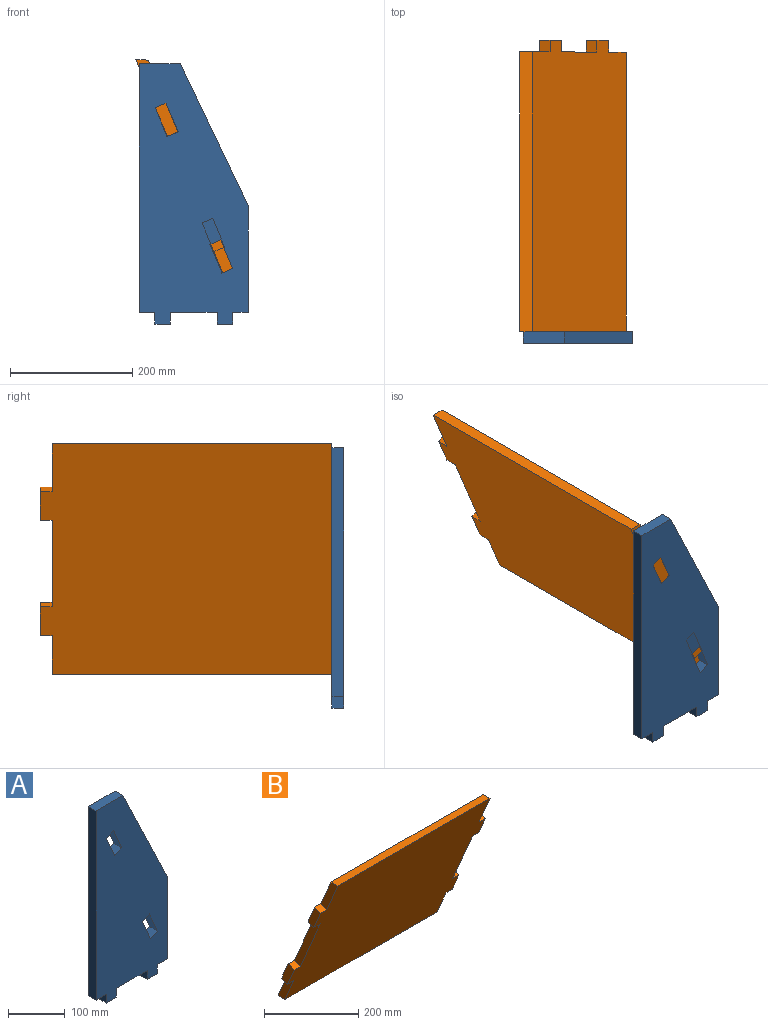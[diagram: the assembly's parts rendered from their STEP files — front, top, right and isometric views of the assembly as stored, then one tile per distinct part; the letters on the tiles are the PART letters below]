
ASSEMBLY  parts=2 mates=1
PART A: 23 faces, bbox 177.9x19.1x425.5 mm
  f0: plane 425.45x177.85mm, normal (0,-1,0), area 58405.1mm2, adj f2,f3,f4,f5,f6,f7,f8,f9
  f1: plane 425.45x177.85mm, normal (0,1,0), area 58405.1mm2, adj f2,f3,f4,f5,f6,f7,f8,f9
  f2: plane 76.25x19.05mm, normal (0,0,-1), area 1452.6mm2, adj f0,f1,f3,f14
  f3: plane 19.05x19.05mm, normal (-1,0,0), area 362.9mm2, adj f0,f1,f2,f4
  f4: plane 25.4x19.05mm, normal (0,0,-1), area 483.9mm2, adj f0,f1,f3,f5
  f5: plane 19.05x19.05mm, normal (1,0,0), area 362.9mm2, adj f0,f1,f4,f6
  f6: plane 25.4x19.05mm, normal (0,0,-1), area 483.9mm2, adj f0,f1,f5,f7
  f7: plane 174.24x19.05mm, normal (1,0,0), area 3319.3mm2, adj f0,f1,f6,f8
  f8: plane 232.16x111.15mm, normal (0.9,0,0.43), area 4903.3mm2, adj f0,f1,f7,f9
  f9: plane 66.7x19.05mm, normal (0,0,1), area 1270.6mm2, adj f0,f1,f8,f10
  f10: plane 406.4x19.05mm, normal (-1,0,0), area 7741.9mm2, adj f0,f1,f9,f11
  f11: plane 25.4x19.05mm, normal (0,0,-1), area 483.9mm2, adj f0,f1,f10,f12
  f12: plane 19.05x19.05mm, normal (-1,0,0), area 362.9mm2, adj f0,f1,f11,f13
  f13: plane 25.4x19.05mm, normal (0,0,-1), area 483.9mm2, adj f0,f1,f12,f14
  f14: plane 19.05x19.05mm, normal (1,0,0), area 362.9mm2, adj f0,f1,f2,f13
  f15: plane 46.81x19.73mm, normal (-0.92,0,-0.39), area 967.7mm2, adj f0,f1,f16,f18
  f16: plane 19.05x17.55mm, normal (0.39,0,-0.92), area 362.9mm2, adj f0,f1,f15,f17
  f17: plane 46.81x19.73mm, normal (0.92,0,0.39), area 967.7mm2, adj f0,f1,f16,f18
  f18: plane 19.05x17.55mm, normal (-0.39,0,0.92), area 362.9mm2, adj f0,f1,f15,f17
  f19: plane 46.66x20.09mm, normal (-0.92,0,-0.4), area 967.7mm2, adj f0,f1,f20,f22
  f20: plane 19.05x17.65mm, normal (0.38,0,-0.93), area 363mm2, adj f0,f1,f19,f21
  f21: plane 47.01x20.25mm, normal (0.92,0,0.4), area 975.1mm2, adj f0,f1,f20,f22
  f22: plane 19.05x17.5mm, normal (-0.4,0,0.92), area 362.9mm2, adj f0,f1,f19,f21
PART B: 22 faces, bbox 495.3x179.5x374.1 mm
  f0: plane 147.73x77.08mm, normal (1,0,0), area 2903.2mm2, adj f5,f7,f17,f19
  f1: plane 77.59x50.47mm, normal (1,0,0), area 1528.6mm2, adj f4,f5,f7,f18
  f2: plane 147.73x77.08mm, normal (-1,0,0), area 2903.2mm2, adj f5,f7,f10,f15
  f3: plane 77.59x50.47mm, normal (-1,0,0), area 1528.6mm2, adj f4,f5,f7,f12
  f4: plane 457.2x20.7mm, normal (0,0,1), area 9461.8mm2, adj f1,f3,f5,f7
  f5: plane 495.3x374.09mm, normal (0,-0.92,-0.39), area 189677mm2, adj f0,f1,f2,f3,f4,f6,f8,f9
  f6: plane 457.2x20.7mm, normal (0,0,-1), area 9461.8mm2, adj f5,f7,f8,f9
  f7: plane 495.3x374.09mm, normal (0,0.92,0.39), area 189677mm2, adj f0,f1,f2,f3,f4,f6,f8,f9
  f8: plane 70.14x47.31mm, normal (1,0,0), area 1374.6mm2, adj f5,f6,f7,f21
  f9: plane 70.14x47.31mm, normal (-1,0,0), area 1374.6mm2, adj f5,f6,f7,f13
  f10: plane 19.05x17.54mm, normal (0,0.39,-0.92), area 362.9mm2, adj f2,f5,f7,f11
  f11: plane 54.21x37.38mm, normal (-1,0,0), area 967.7mm2, adj f5,f7,f10,f12
  f12: plane 19.05x17.54mm, normal (0,-0.39,0.92), area 362.9mm2, adj f3,f5,f7,f11
  f13: plane 19.05x17.54mm, normal (0,0.39,-0.92), area 362.9mm2, adj f5,f7,f9,f14
  f14: plane 54.21x37.38mm, normal (-1,0,0), area 967.7mm2, adj f5,f7,f13,f15
  f15: plane 19.05x17.54mm, normal (0,-0.39,0.92), area 362.9mm2, adj f2,f5,f7,f14
  f16: plane 54.21x37.38mm, normal (1,0,0), area 967.7mm2, adj f5,f7,f17,f18
  f17: plane 19.05x17.54mm, normal (0,0.39,-0.92), area 362.9mm2, adj f0,f5,f7,f16
  f18: plane 19.05x17.54mm, normal (0,-0.39,0.92), area 362.9mm2, adj f1,f5,f7,f16
  f19: plane 19.05x17.54mm, normal (0,-0.39,0.92), area 362.9mm2, adj f0,f5,f7,f20
  f20: plane 54.21x37.38mm, normal (1,0,0), area 967.7mm2, adj f5,f7,f19,f21
  f21: plane 19.05x17.54mm, normal (0,0.39,-0.92), area 362.9mm2, adj f5,f7,f8,f20
PLACE A t=(-243.57,69.13,373.38)mm
PLACE B rot(axis=(-0.01,0.01,-1),90deg) t=(-219.11,550.71,173.45)mm
MATE slider B.f18 <-> A.f20  axis (-0.38,0,0.93) through (-293.37,59.6,494.89)mm
